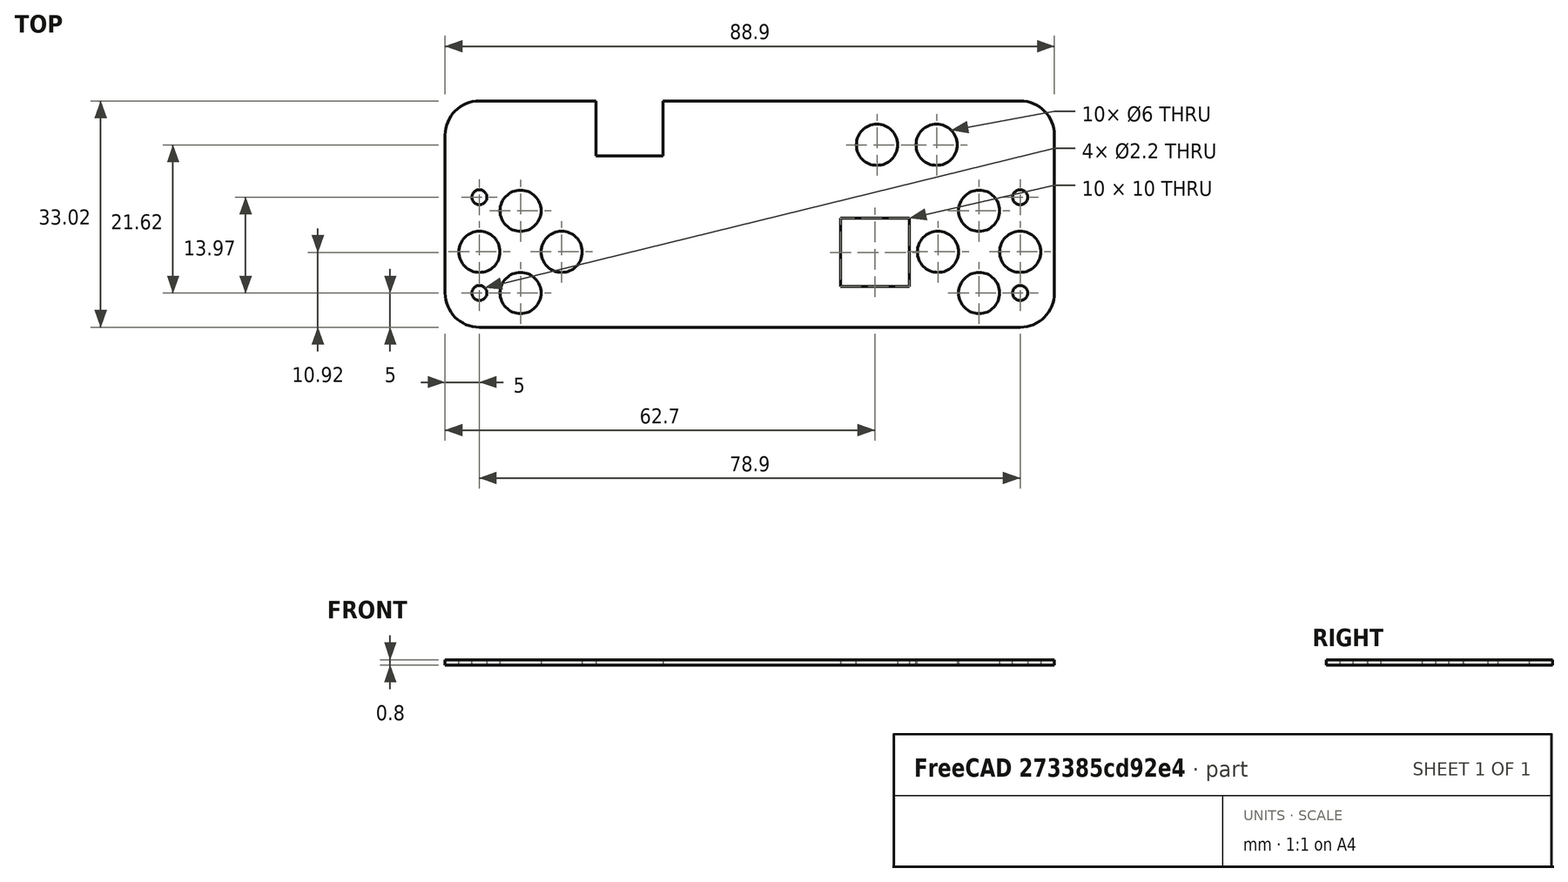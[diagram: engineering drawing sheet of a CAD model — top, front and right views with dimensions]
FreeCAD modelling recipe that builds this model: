
FCSTD DOCUMENT  (FreeCAD 1.0R39285 (Git))
Label: PIX6T4_Color_top
License: All rights reserved
LicenseURL: http://en.wikipedia.org/wiki/All_rights_reserved
objects: App::Part×3, PartDesign::CoordinateSystem×1, Part::Feature×1, Sketcher::SketchObject×1
note: 4 computed .brp shape members not serialized (recipe doc carries the construction recipe); baked Part::Feature solids carry a one-line shape summary decoded from their .brp

FEATURE [PartDesign::CoordinateSystem] Local_CS_83e9
  AttacherType = Attacher::AttachEngine3D
  MapMode = 2
FEATURE [Part::Feature] Pcb_83e9
  Placement = pos=(-194.45,116.51,0) rot=(0,0,1;0rad)
  shape: bbox 88.9 x 33.02 x 0.8 mm, 32 faces (baked)
FEATURE [Sketcher::SketchObject] PCB_Sketch_83e9
  ArcFitTolerance = 1e-06
  FullyConstrained = false
  MakeInternals = false
  sketch-geometry (16):
    g0: LineSegment StartX=-44.45 StartY=-11.51 StartZ=0 EndX=-44.45 EndY=11.51 EndZ=0
    g1: LineSegment StartX=-12.65 StartY=16.51 StartZ=0 EndX=-12.65 EndY=8.46 EndZ=0
    g2: LineSegment StartX=-22.45 StartY=8.46 StartZ=0 EndX=-12.65 EndY=8.46 EndZ=0
    g3: LineSegment StartX=-39.45 StartY=16.51 StartZ=0 EndX=-22.45 EndY=16.51 EndZ=0
    g4: LineSegment StartX=44.45 StartY=11.51 StartZ=0 EndX=44.45 EndY=-11.51 EndZ=0
    g5: LineSegment StartX=-12.65 StartY=16.51 StartZ=0 EndX=39.45 EndY=16.51 EndZ=0
    g6: LineSegment StartX=-22.45 StartY=16.51 StartZ=0 EndX=-22.45 EndY=8.46 EndZ=0
    g7: LineSegment StartX=39.45 StartY=-16.51 StartZ=0 EndX=-39.45 EndY=-16.51 EndZ=0
    g8: LineSegment StartX=13.25 StartY=-0.59 StartZ=0 EndX=23.25 EndY=-0.59 EndZ=0
    g9: LineSegment StartX=23.25 StartY=-0.59 StartZ=0 EndX=23.25 EndY=-10.59 EndZ=0
    g10: LineSegment StartX=23.25 StartY=-10.59 StartZ=0 EndX=13.25 EndY=-10.59 EndZ=0
    g11: LineSegment StartX=13.25 StartY=-10.59 StartZ=0 EndX=13.25 EndY=-0.59 EndZ=0
    g12: ArcOfCircle CenterX=39.45 CenterY=11.51 CenterZ=0 NormalX=0 NormalY=0 NormalZ=-1 AngleXU=1.5708 Radius=5 StartAngle=0 EndAngle=1.5708
    g13: ArcOfCircle CenterX=-39.45 CenterY=11.51 CenterZ=0 NormalX=0 NormalY=0 NormalZ=-1 AngleXU=-6.42331e-08 Radius=5 StartAngle=0 EndAngle=1.5708
    g14: ArcOfCircle CenterX=-39.45 CenterY=-11.51 CenterZ=0 NormalX=0 NormalY=0 NormalZ=-1 AngleXU=-1.5708 Radius=5 StartAngle=0 EndAngle=1.5708
    g15: ArcOfCircle CenterX=39.45 CenterY=-11.51 CenterZ=0 NormalX=0 NormalY=0 NormalZ=-1 AngleXU=3.14159 Radius=5 StartAngle=0 EndAngle=1.5708
FEATURE [App::Part] Board_Geoms_83e9
  Group = -> [Pcb_83e9,PCB_Sketch_83e9]
  Origin = -> Origin
FEATURE [App::Part] Step_Models_83e9
  Origin = -> Origin002
FEATURE [App::Part] Board_83e9  label="PIX6T4_Color_top"
  Group = -> [Local_CS_83e9,Board_Geoms_83e9,Step_Models_83e9]
  Origin = -> Origin001
